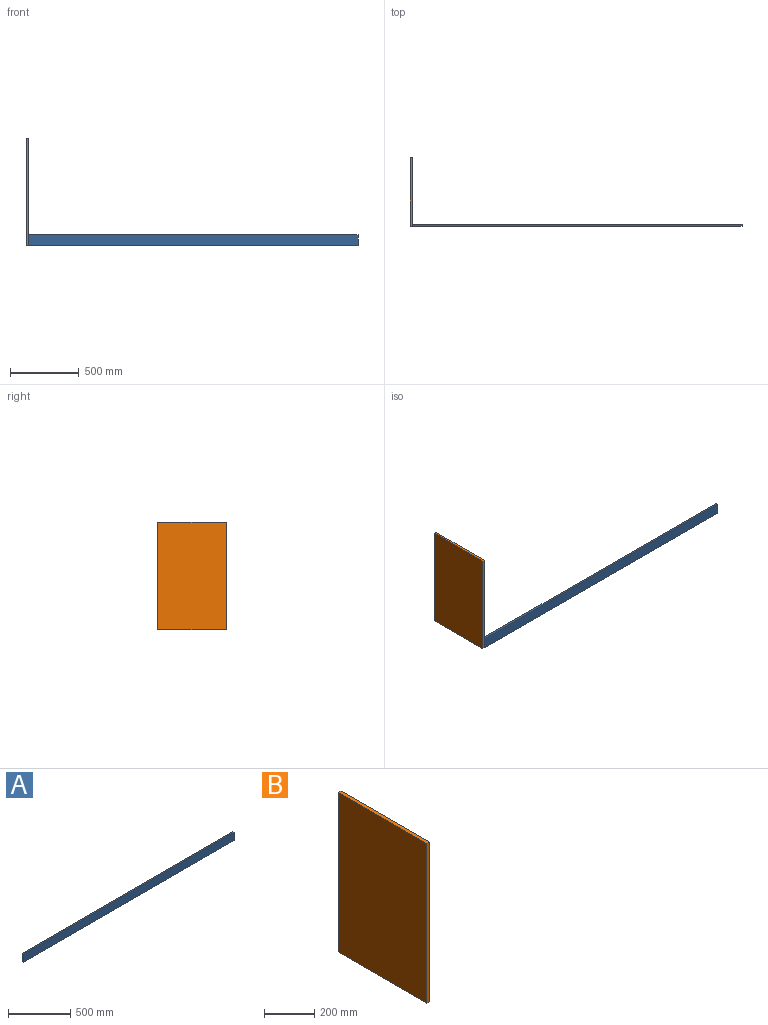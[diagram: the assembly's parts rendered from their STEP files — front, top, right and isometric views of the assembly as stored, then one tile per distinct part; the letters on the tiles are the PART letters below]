
ASSEMBLY  parts=2 mates=1
PART A: 6 faces, bbox 2400x15x80 mm
  f0: plane 80x15mm, normal (-1,0,0), area 1200mm2, adj f1,f3,f4,f5
  f1: plane 2400x80mm, normal (0,-1,0), area 192000mm2, adj f0,f2,f4,f5
  f2: plane 80x15mm, normal (1,0,0), area 1200mm2, adj f1,f3,f4,f5
  f3: plane 2400x80mm, normal (0,1,0), area 192000mm2, adj f0,f2,f4,f5
  f4: plane 2400x15mm, normal (0,0,1), area 36000mm2, adj f0,f1,f2,f3
  f5: plane 2400x15mm, normal (0,0,-1), area 36000mm2, adj f0,f1,f2,f3
PART B: 6 faces, bbox 15x500x780 mm
  f0: plane 780x500mm, normal (-1,0,0), area 390000mm2, adj f1,f3,f4,f5
  f1: plane 780x15mm, normal (0,-1,0), area 11700mm2, adj f0,f2,f4,f5
  f2: plane 780x500mm, normal (1,0,0), area 390000mm2, adj f1,f3,f4,f5
  f3: plane 780x15mm, normal (0,1,0), area 11700mm2, adj f0,f2,f4,f5
  f4: plane 500x15mm, normal (0,0,1), area 7500mm2, adj f0,f1,f2,f3
  f5: plane 500x15mm, normal (0,0,-1), area 7500mm2, adj f0,f1,f2,f3
PLACE A t=(123.08,827.59,79.81)mm
PLACE B t=(108.08,827.59,79.81)mm
MATE planar A.f5 <-> B.f5  axis (0,0,-1) through (123.08,827.59,79.81)mm
